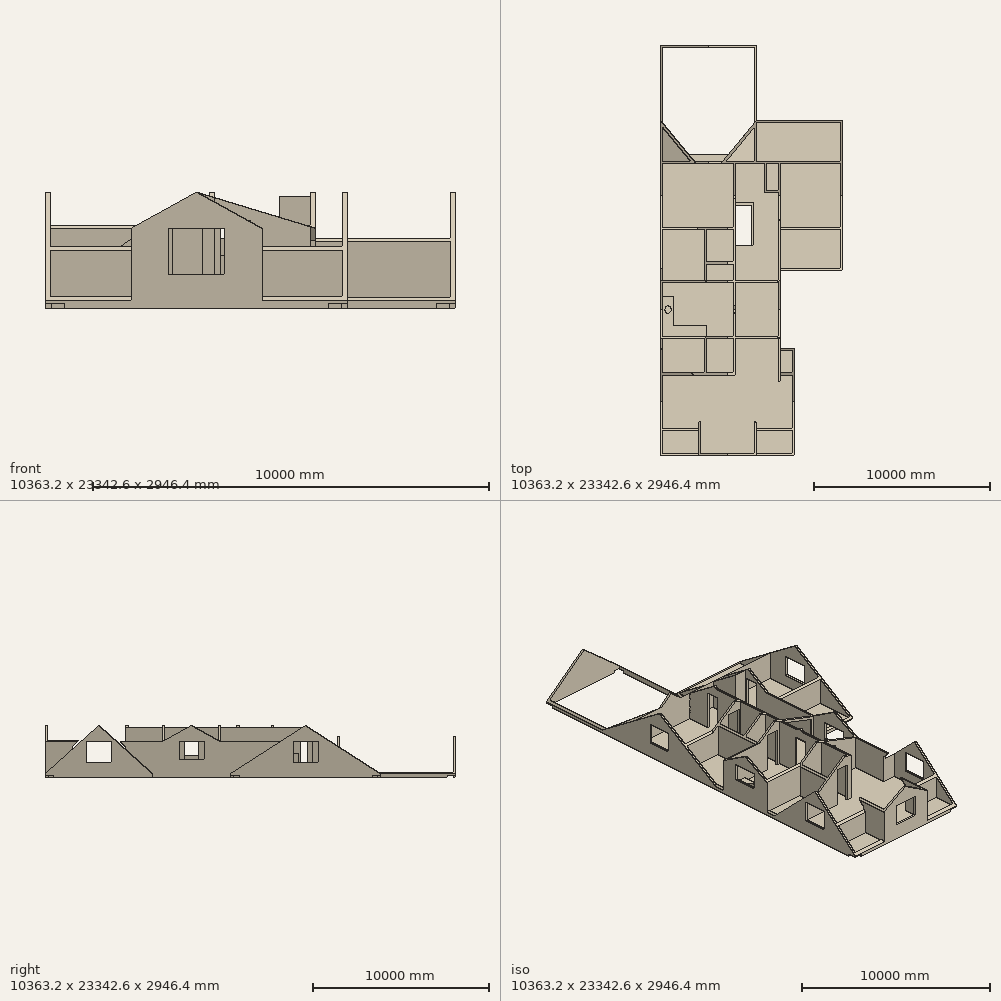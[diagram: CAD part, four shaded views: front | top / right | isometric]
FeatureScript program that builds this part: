
annotation { "Feature Type Name" : "Feature", "Feature Type Description" : "" }
export const myFeature = defineFeature(function(context is Context, id is Id, definition is map)
    precondition{}
    {
        {
            var Q0;
            Q0=qCreatedBy(makeId("Top.planeOp"),FACE);
            cPlane(context, id + "F0", {"entities" : qUnion([Q0]), "cplaneType" : CPlaneType.OFFSET, "offset" : 2946.4 * mm, "width" : 152.4 * mm, "height" : 152.4 * mm});
        }
        {
            var Q0;
            Q0=qCreatedBy(makeId("Top.planeOp"),FACE);
            var sketch = newSketch(context, id + "F1", { "sketchPlane" : qUnion([Q0])});
            skLineSegment(sketch, "E0", {"start": v(0, 0) * mm, "end": v(7645.4, 0) * mm});
            skLineSegment(sketch, "E1", {"start": v(7645.4, 0) * mm, "end": v(7645.4, 6096) * mm});
            skLineSegment(sketch, "E2", {"start": v(7645.4, 6096) * mm, "end": v(6832.6, 6096) * mm});
            skLineSegment(sketch, "E3", {"start": v(6832.6, 6096) * mm, "end": v(6832.6, 10541) * mm});
            skLineSegment(sketch, "E4", {"start": v(6832.6, 10541) * mm, "end": v(10363.2, 10541) * mm});
            skLineSegment(sketch, "E5", {"start": v(10363.2, 10541) * mm, "end": v(10363.2, 19075.4) * mm});
            skLineSegment(sketch, "E6", {"start": v(10363.2, 19075.4) * mm, "end": v(5486.4, 19075.4) * mm});
            skLineSegment(sketch, "E7", {"start": v(5486.4, 19075.4) * mm, "end": v(5486.4, 23342.6) * mm});
            skLineSegment(sketch, "E8", {"start": v(5486.4, 23342.6) * mm, "end": v(0, 23342.6) * mm});
            skLineSegment(sketch, "E9", {"start": v(0, 23342.6) * mm, "end": v(0, 0) * mm});
            skSolve(sketch);
        }
        {
            var Q0;
            Q0 = qSketchRegion(id + "F1", true);
            extrude(context, id + "F2", {"entities" : qUnion([Q0]), "depth" : 2946.4 * mm});
        }
        {
            var Q0;
            Q0=makeQuery(id+"F2.opExtrude","SWEPT_FACE",FACE,{"disambiguationData":[OSD([sQuery(id+"F1.wireOp",EDGE,"E5")])]});
            var sketch = newSketch(context, id + "F3", { "sketchPlane" : qUnion([Q0])});
            skLineSegment(sketch, "E10", {"start": v(10541, 203.2) * mm, "end": v(19075.4, 203.2) * mm, "construction": true});
            skLineSegment(sketch, "E11", {"start": v(14808.2, 203.2) * mm, "end": v(14808.2, 2946.4) * mm, "construction": true});
            skLineSegment(sketch, "E12", {"start": v(10541, 203.2) * mm, "end": v(14808.2, 2946.4) * mm});
            skLineSegment(sketch, "E13", {"start": v(10541, 203.2) * mm, "end": v(10541, 2946.4) * mm});
            skLineSegment(sketch, "E14", {"start": v(10541, 2946.4) * mm, "end": v(19075.4, 2946.4) * mm});
            skLineSegment(sketch, "E15", {"start": v(19075.4, 2946.4) * mm, "end": v(19075.4, 203.2) * mm});
            skLineSegment(sketch, "E16", {"start": v(19075.4, 203.2) * mm, "end": v(14808.2, 2946.4) * mm});
            skLineSegment(sketch, "E17", {"start": v(6096, 203.2) * mm, "end": v(0, 203.2) * mm, "construction": true});
            skLineSegment(sketch, "E18", {"start": v(3048, 203.2) * mm, "end": v(3048, 2946.4) * mm, "construction": true});
            skLineSegment(sketch, "E19", {"start": v(3048, 2946.4) * mm, "end": v(0, 203.2) * mm});
            skLineSegment(sketch, "E20", {"start": v(0, 203.2) * mm, "end": v(0, 2946.4) * mm});
            skLineSegment(sketch, "E21", {"start": v(0, 2946.4) * mm, "end": v(6096, 2946.4) * mm});
            skLineSegment(sketch, "E22", {"start": v(6096, 2946.4) * mm, "end": v(6096, 203.2) * mm});
            skLineSegment(sketch, "E23", {"start": v(6096, 203.2) * mm, "end": v(3048, 2946.4) * mm});
            skSolve(sketch);
        }
        {
            var Q0;
            Q0 = qSketchRegion(id + "F3", true);
            extrude(context, id + "F4", {"entities" : qUnion([Q0]), "operationType" : NewBodyOperationType.REMOVE, "endBound" : BoundingType.THROUGH_ALL, "oppositeDirection" : true, "depth" : 25.4 * mm});
        }
        {
            var Q0;
            Q0=makeQuery(id+"F2.opExtrude","SWEPT_FACE",FACE,{"disambiguationData":[OSD([sQuery(id+"F1.wireOp",EDGE,"E8")])]});
            var sketch = newSketch(context, id + "F5", { "sketchPlane" : qUnion([Q0])});
            skLineSegment(sketch, "E24", {"start": v(-5486.4, 203.2) * mm, "end": v(0, 203.2) * mm, "construction": true});
            skLineSegment(sketch, "E25", {"start": v(-2743.2, 203.2) * mm, "end": v(-2743.2, 2336.8) * mm, "construction": true});
            skLineSegment(sketch, "E26", {"start": v(-5486.4, 203.2) * mm, "end": v(-2743.2, 2336.8) * mm});
            skLineSegment(sketch, "E27", {"start": v(-2743.2, 2336.8) * mm, "end": v(0, 203.2) * mm});
            skLineSegment(sketch, "E28", {"start": v(-5486.4, 203.2) * mm, "end": v(-5486.4, 2946.4) * mm});
            skLineSegment(sketch, "E29", {"start": v(-5486.4, 2946.4) * mm, "end": v(0, 2946.4) * mm});
            skLineSegment(sketch, "E30", {"start": v(0, 2946.4) * mm, "end": v(0, 203.2) * mm});
            skSolve(sketch);
        }
        {
            var Q0;
            Q0 = qSketchRegion(id + "F5", true);
            extrude(context, id + "F6", {"entities" : qUnion([Q0]), "operationType" : NewBodyOperationType.REMOVE, "oppositeDirection" : true, "depth" : 4267.2 * mm});
        }
        {
            var Q0;
            Q0=makeQuery(id+"F4.boolean.opBoolean","COPY",FACE,{"derivedFrom":makeQuery(id+"F4.opExtrude","SWEPT_FACE",FACE,{"disambiguationData":[OSD([sQuery(id+"F3.wireOp",EDGE,"E15")])]})});
            var sketch = newSketch(context, id + "F7", { "sketchPlane" : qUnion([Q0])});
            skLineSegment(sketch, "E31", {"start": v(0, 203.2) * mm, "end": v(2743.2, 2336.8) * mm});
            skLineSegment(sketch, "E32", {"start": v(2743.2, 2336.8) * mm, "end": v(5486.4, 203.2) * mm});
            skLineSegment(sketch, "E33", {"start": v(5486.4, 203.2) * mm, "end": v(0, 203.2) * mm});
            skSolve(sketch);
        }
        {
            var Q0;
            Q0 = qSketchRegion(id + "F7", true);
            extrude(context, id + "F8", {"entities" : qUnion([Q0]), "operationType" : NewBodyOperationType.ADD, "endBound" : BoundingType.UP_TO_NEXT, "depth" : 25.4 * mm});
        }
        {
            var Q0;
            Q0=makeQuery(id+"F4.boolean.opBoolean","COPY",FACE,{"derivedFrom":makeQuery(id+"F4.opExtrude","SWEPT_FACE",FACE,{"disambiguationData":[OSD([sQuery(id+"F3.wireOp",EDGE,"E22")])]})});
            var sketch = newSketch(context, id + "F9", { "sketchPlane" : qUnion([Q0])});
            skLineSegment(sketch, "E34", {"start": v(0, 203.2) * mm, "end": v(6832.6, 203.2) * mm, "construction": true});
            skLineSegment(sketch, "E35", {"start": v(3822.7, 203.2) * mm, "end": v(3822.7, 2946.4) * mm, "construction": true});
            skLineSegment(sketch, "E36", {"start": v(6832.6, 203.2) * mm, "end": v(6832.6, 2032) * mm, "construction": true});
            skLineSegment(sketch, "E37", {"start": v(0, 203.2) * mm, "end": v(3822.7, 2946.4) * mm});
            skLineSegment(sketch, "E38", {"start": v(3822.7, 2946.4) * mm, "end": v(6832.6, 2032) * mm});
            skLineSegment(sketch, "E39", {"start": v(6832.6, 2032) * mm, "end": v(6832.6, 2946.4) * mm});
            skLineSegment(sketch, "E40", {"start": v(6832.6, 2946.4) * mm, "end": v(0, 2946.4) * mm});
            skLineSegment(sketch, "E41", {"start": v(0, 2946.4) * mm, "end": v(0, 203.2) * mm});
            skSolve(sketch);
        }
        {
            var Q0;
            Q0 = qSketchRegion(id + "F9", true);
            extrude(context, id + "F10", {"entities" : qUnion([Q0]), "operationType" : NewBodyOperationType.REMOVE, "oppositeDirection" : true, "depth" : 4445 * mm});
        }
        {
            var Q0;
            Q0=makeQuery(id+"F4.boolean.opBoolean","COPY",FACE,{"derivedFrom":makeQuery(id+"F4.opExtrude","SWEPT_FACE",FACE,{"disambiguationData":[OSD([sQuery(id+"F3.wireOp",EDGE,"E13")])]})});
            var sketch = newSketch(context, id + "F11", { "sketchPlane" : qUnion([Q0])});
            skLineSegment(sketch, "E42", {"start": v(0, 203.2) * mm, "end": v(-6832.6, 203.2) * mm});
            skLineSegment(sketch, "E43", {"start": v(-6832.6, 203.2) * mm, "end": v(-6832.6, 2032) * mm});
            skLineSegment(sketch, "E44", {"start": v(-6832.6, 2032) * mm, "end": v(-3822.7, 2946.4) * mm});
            skLineSegment(sketch, "E45", {"start": v(-3822.7, 2946.4) * mm, "end": v(0, 203.2) * mm});
            skSolve(sketch);
        }
        {
            var Q0;
            Q0 = qSketchRegion(id + "F11", true);
            extrude(context, id + "F12", {"entities" : qUnion([Q0]), "operationType" : NewBodyOperationType.ADD, "endBound" : BoundingType.UP_TO_NEXT, "depth" : 25.4 * mm});
        }
        {
            var Q0;
            Q0=makeQuery(id+"F4.boolean.opBoolean","COPY",FACE,{"derivedFrom":makeQuery(id+"F4.opExtrude","SWEPT_FACE",FACE,{"disambiguationData":[OSD([sQuery(id+"F3.wireOp",EDGE,"E22")])]})});
            var sketch = newSketch(context, id + "F13", { "sketchPlane" : qUnion([Q0])});
            skLineSegment(sketch, "E46", {"start": v(0, 203.2) * mm, "end": v(3822.7, 2946.4) * mm});
            skLineSegment(sketch, "E47", {"start": v(3822.7, 2946.4) * mm, "end": v(6832.6, 2032) * mm});
            skLineSegment(sketch, "E48", {"start": v(6832.6, 2032) * mm, "end": v(6832.6, 203.2) * mm});
            skLineSegment(sketch, "E49", {"start": v(6832.6, 203.2) * mm, "end": v(0, 203.2) * mm});
            skSolve(sketch);
        }
        {
            var Q0;
            Q0 = qSketchRegion(id + "F13", true);
            extrude(context, id + "F14", {"entities" : qUnion([Q0]), "operationType" : NewBodyOperationType.ADD, "endBound" : BoundingType.UP_TO_NEXT, "depth" : 25.4 * mm});
        }
        {
            var Q0;
            Q0=makeQuery(id+"F14.boolean.opBoolean","MERGE",FACE,{"derivedFrom":[makeQuery(id+"F12.boolean.opBoolean","MERGE",FACE,{"derivedFrom":[makeQuery(id+"F2.opExtrude","SWEPT_FACE",FACE,{"disambiguationData":[OSD([sQuery(id+"F1.wireOp",EDGE,"E3")])]}),makeQuery(id+"F12.opExtrude","SWEPT_FACE",FACE,{"disambiguationData":[OSD([sQuery(id+"F11.wireOp",EDGE,"E43")])]})]}),makeQuery(id+"F14.opExtrude","SWEPT_FACE",FACE,{"disambiguationData":[OSD([sQuery(id+"F13.wireOp",EDGE,"E48")])]})]});
            var sketch = newSketch(context, id + "F15", { "sketchPlane" : qUnion([Q0])});
            skLineSegment(sketch, "E50", {"start": v(6667.5, 203.2) * mm, "end": v(9969.5, 203.2) * mm, "construction": true});
            skLineSegment(sketch, "E51", {"start": v(8318.5, 203.2) * mm, "end": v(8318.5, 2946.4) * mm, "construction": true});
            skLineSegment(sketch, "E52", {"start": v(6667.5, 203.2) * mm, "end": v(6667.5, 2032) * mm, "construction": true});
            skLineSegment(sketch, "E53", {"start": v(6667.5, 2032) * mm, "end": v(8318.5, 2946.4) * mm});
            skLineSegment(sketch, "E54.MirrorCS", {"start": v(9969.5, 2032) * mm, "end": v(8318.5, 2946.4) * mm});
            skLineSegment(sketch, "E55", {"start": v(6667.5, 2032) * mm, "end": v(9969.5, 2032) * mm});
            skSolve(sketch);
        }
        {
            var Q0;
            Q0 = qSketchRegion(id + "F15", true);
            extrude(context, id + "F16", {"entities" : qUnion([Q0]), "operationType" : NewBodyOperationType.ADD, "endBound" : BoundingType.UP_TO_NEXT, "oppositeDirection" : true, "depth" : 25.4 * mm});
        }
        {
            var Q0;
            Q0=makeQuery(id+"F2.opExtrude","SWEPT_FACE",FACE,{"disambiguationData":[OSD([sQuery(id+"F1.wireOp",EDGE,"E9")])]});
            var sketch = newSketch(context, id + "F17", { "sketchPlane" : qUnion([Q0])});
            skLineSegment(sketch, "E56", {"start": v(-9969.5, 203.2) * mm, "end": v(-6667.5, 203.2) * mm});
            skLineSegment(sketch, "E57", {"start": v(-8318.5, 203.2) * mm, "end": v(-8318.5, 2946.4) * mm, "construction": true});
            skLineSegment(sketch, "E58", {"start": v(-9969.5, 203.2) * mm, "end": v(-9969.5, 2032) * mm});
            skLineSegment(sketch, "E59", {"start": v(-9969.5, 2032) * mm, "end": v(-8318.5, 2946.4) * mm});
            skLineSegment(sketch, "E60.MirrorCS", {"start": v(-6667.5, 203.2) * mm, "end": v(-6667.5, 2032) * mm});
            skLineSegment(sketch, "E61.MirrorCS", {"start": v(-6667.5, 2032) * mm, "end": v(-8318.5, 2946.4) * mm});
            skSolve(sketch);
        }
        {
            var Q0;
            Q0 = qSketchRegion(id + "F17", true);
            extrude(context, id + "F18", {"entities" : qUnion([Q0]), "operationType" : NewBodyOperationType.ADD, "endBound" : BoundingType.UP_TO_NEXT, "oppositeDirection" : true, "depth" : 25.4 * mm});
        }
        {
            var Q0;
            Q0=makeQuery(id+"F2.opExtrude","SWEPT_FACE",FACE,{"disambiguationData":[OSD([sQuery(id+"F1.wireOp",EDGE,"E0")])]});
            var sketch = newSketch(context, id + "F19", { "sketchPlane" : qUnion([Q0])});
            skLineSegment(sketch, "E62", {"start": v(2171.7, 203.2) * mm, "end": v(5473.7, 203.2) * mm});
            skLineSegment(sketch, "E63", {"start": v(3822.7, 203.2) * mm, "end": v(3822.7, 2946.4) * mm, "construction": true});
            skLineSegment(sketch, "E64", {"start": v(2171.7, 203.2) * mm, "end": v(2171.7, 2032) * mm});
            skLineSegment(sketch, "E65", {"start": v(2171.7, 2032) * mm, "end": v(3822.7, 2946.4) * mm});
            skLineSegment(sketch, "E66.MirrorCS", {"start": v(5473.7, 203.2) * mm, "end": v(5473.7, 2032) * mm});
            skLineSegment(sketch, "E67.MirrorCS", {"start": v(5473.7, 2032) * mm, "end": v(3822.7, 2946.4) * mm});
            skSolve(sketch);
        }
        {
            var Q0;
            Q0 = qSketchRegion(id + "F19", true);
            extrude(context, id + "F20", {"entities" : qUnion([Q0]), "operationType" : NewBodyOperationType.ADD, "endBound" : BoundingType.UP_TO_NEXT, "oppositeDirection" : true, "depth" : 25.4 * mm});
        }
        {
            var Q0;
            Q0=qCreatedBy(id+"F0.planeOp",FACE);
            var sketch = newSketch(context, id + "F21", { "sketchPlane" : qUnion([Q0])});
            skLineSegment(sketch, "E68.bottom", {"start": v(127, 23215.6) * mm, "end": v(5359.4, 23215.6) * mm});
            skLineSegment(sketch, "E68.top", {"start": v(127, 16764) * mm, "end": v(5359.4, 16764) * mm});
            skLineSegment(sketch, "E68.left", {"start": v(127, 23215.6) * mm, "end": v(127, 16764) * mm});
            skLineSegment(sketch, "E68.right", {"start": v(5359.4, 23215.6) * mm, "end": v(5359.4, 16764) * mm});
            skLineSegment(sketch, "E69.bottom", {"start": v(5486.4, 18948.4) * mm, "end": v(10236.2, 18948.4) * mm});
            skLineSegment(sketch, "E69.top", {"start": v(5486.4, 16764) * mm, "end": v(10236.2, 16764) * mm});
            skLineSegment(sketch, "E69.left", {"start": v(5486.4, 18948.4) * mm, "end": v(5486.4, 16764) * mm});
            skLineSegment(sketch, "E69.right", {"start": v(10236.2, 18948.4) * mm, "end": v(10236.2, 16764) * mm});
            skLineSegment(sketch, "E70.bottom", {"start": v(6832.6, 16637) * mm, "end": v(10236.2, 16637) * mm});
            skLineSegment(sketch, "E70.top", {"start": v(6832.6, 12979.4) * mm, "end": v(10236.2, 12979.4) * mm});
            skLineSegment(sketch, "E70.left", {"start": v(6832.6, 16637) * mm, "end": v(6832.6, 12979.4) * mm});
            skLineSegment(sketch, "E70.right", {"start": v(10236.2, 16637) * mm, "end": v(10236.2, 12979.4) * mm});
            skLineSegment(sketch, "E71.bottom", {"start": v(6832.6, 12852.4) * mm, "end": v(10236.2, 12852.4) * mm});
            skLineSegment(sketch, "E71.top", {"start": v(6832.6, 10668) * mm, "end": v(10236.2, 10668) * mm});
            skLineSegment(sketch, "E71.left", {"start": v(6832.6, 12852.4) * mm, "end": v(6832.6, 10668) * mm});
            skLineSegment(sketch, "E71.right", {"start": v(10236.2, 12852.4) * mm, "end": v(10236.2, 10668) * mm});
            skLineSegment(sketch, "E72.bottom", {"start": v(6032.5, 16637) * mm, "end": v(6705.6, 16637) * mm});
            skLineSegment(sketch, "E72.top", {"start": v(6032.5, 15113) * mm, "end": v(6705.6, 15113) * mm});
            skLineSegment(sketch, "E72.left", {"start": v(6032.5, 16637) * mm, "end": v(6032.5, 15113) * mm});
            skLineSegment(sketch, "E72.right", {"start": v(6705.6, 16637) * mm, "end": v(6705.6, 15113) * mm});
            skLineSegment(sketch, "E73.bottom", {"start": v(127, 16637) * mm, "end": v(4140.2, 16637) * mm});
            skLineSegment(sketch, "E73.top", {"start": v(127, 12979.4) * mm, "end": v(4140.2, 12979.4) * mm});
            skLineSegment(sketch, "E73.left", {"start": v(127, 16637) * mm, "end": v(127, 12979.4) * mm});
            skLineSegment(sketch, "E73.right", {"start": v(4140.2, 16637) * mm, "end": v(4140.2, 12979.4) * mm});
            skLineSegment(sketch, "E74.bottom", {"start": v(127, 12852.4) * mm, "end": v(2489.2, 12852.4) * mm});
            skLineSegment(sketch, "E74.top", {"start": v(127, 9969.5) * mm, "end": v(2489.2, 9969.5) * mm});
            skLineSegment(sketch, "E74.left", {"start": v(127, 12852.4) * mm, "end": v(127, 9969.5) * mm});
            skLineSegment(sketch, "E74.right", {"start": v(2489.2, 12852.4) * mm, "end": v(2489.2, 9969.5) * mm});
            skLineSegment(sketch, "E75.bottom", {"start": v(2616.2, 12852.4) * mm, "end": v(4140.2, 12852.4) * mm});
            skLineSegment(sketch, "E75.top", {"start": v(2616.2, 11023.6) * mm, "end": v(4140.2, 11023.6) * mm});
            skLineSegment(sketch, "E75.left", {"start": v(2616.2, 12852.4) * mm, "end": v(2616.2, 11023.6) * mm});
            skLineSegment(sketch, "E75.right", {"start": v(4140.2, 12852.4) * mm, "end": v(4140.2, 11023.6) * mm});
            skLineSegment(sketch, "E76.bottom", {"start": v(2616.2, 10896.6) * mm, "end": v(4140.2, 10896.6) * mm});
            skLineSegment(sketch, "E76.top", {"start": v(2616.2, 9969.5) * mm, "end": v(4140.2, 9969.5) * mm});
            skLineSegment(sketch, "E76.left", {"start": v(2616.2, 10896.6) * mm, "end": v(2616.2, 9969.5) * mm});
            skLineSegment(sketch, "E76.right", {"start": v(4140.2, 10896.6) * mm, "end": v(4140.2, 9969.5) * mm});
            skLineSegment(sketch, "E77.bottom", {"start": v(127, 9842.5) * mm, "end": v(4140.2, 9842.5) * mm});
            skLineSegment(sketch, "E77.top", {"start": v(127, 6794.5) * mm, "end": v(4140.2, 6794.5) * mm});
            skLineSegment(sketch, "E77.left", {"start": v(127, 9842.5) * mm, "end": v(127, 6794.5) * mm});
            skLineSegment(sketch, "E77.right", {"start": v(4140.2, 9842.5) * mm, "end": v(4140.2, 6794.5) * mm});
            skLineSegment(sketch, "E78.bottom", {"start": v(127, 6667.5) * mm, "end": v(2489.2, 6667.5) * mm});
            skLineSegment(sketch, "E78.top", {"start": v(127, 4699) * mm, "end": v(2489.2, 4699) * mm});
            skLineSegment(sketch, "E78.left", {"start": v(127, 6667.5) * mm, "end": v(127, 4699) * mm});
            skLineSegment(sketch, "E78.right", {"start": v(2489.2, 6667.5) * mm, "end": v(2489.2, 4699) * mm});
            skLineSegment(sketch, "E79.bottom", {"start": v(2616.2, 6667.5) * mm, "end": v(4140.2, 6667.5) * mm});
            skLineSegment(sketch, "E79.top", {"start": v(2616.2, 4699) * mm, "end": v(4140.2, 4699) * mm});
            skLineSegment(sketch, "E79.left", {"start": v(2616.2, 6667.5) * mm, "end": v(2616.2, 4699) * mm});
            skLineSegment(sketch, "E79.right", {"start": v(4140.2, 6667.5) * mm, "end": v(4140.2, 4699) * mm});
            skLineSegment(sketch, "E80.bottom", {"start": v(127, 1397) * mm, "end": v(2171.7, 1397) * mm});
            skLineSegment(sketch, "E80.top", {"start": v(127, 127) * mm, "end": v(2171.7, 127) * mm});
            skLineSegment(sketch, "E80.left", {"start": v(127, 1397) * mm, "end": v(127, 127) * mm});
            skLineSegment(sketch, "E80.right", {"start": v(2171.7, 1397) * mm, "end": v(2171.7, 127) * mm});
            skLineSegment(sketch, "E81.bottom", {"start": v(5473.7, 1397) * mm, "end": v(7518.4, 1397) * mm});
            skLineSegment(sketch, "E81.top", {"start": v(5473.7, 127) * mm, "end": v(7518.4, 127) * mm});
            skLineSegment(sketch, "E81.left", {"start": v(5473.7, 1397) * mm, "end": v(5473.7, 127) * mm});
            skLineSegment(sketch, "E81.right", {"start": v(7518.4, 1397) * mm, "end": v(7518.4, 127) * mm});
            skLineSegment(sketch, "E82.bottom", {"start": v(6832.6, 5969) * mm, "end": v(7518.4, 5969) * mm});
            skLineSegment(sketch, "E82.top", {"start": v(6832.6, 4699) * mm, "end": v(7518.4, 4699) * mm});
            skLineSegment(sketch, "E82.left", {"start": v(6832.6, 5969) * mm, "end": v(6832.6, 4699) * mm});
            skLineSegment(sketch, "E82.right", {"start": v(7518.4, 5969) * mm, "end": v(7518.4, 4699) * mm});
            skLineSegment(sketch, "E83", {"start": v(127, 4572) * mm, "end": v(127, 1524) * mm});
            skLineSegment(sketch, "E84", {"start": v(127, 1524) * mm, "end": v(2298.7, 1524) * mm});
            skLineSegment(sketch, "E85", {"start": v(7518.4, 1524) * mm, "end": v(7518.4, 4572) * mm});
            skLineSegment(sketch, "E86", {"start": v(7518.4, 4572) * mm, "end": v(6705.6, 4572) * mm});
            skLineSegment(sketch, "E87", {"start": v(6705.6, 4572) * mm, "end": v(6705.6, 6667.5) * mm});
            skLineSegment(sketch, "E88", {"start": v(6705.6, 6667.5) * mm, "end": v(4267.2, 6667.5) * mm});
            skLineSegment(sketch, "E89", {"start": v(4267.2, 6667.5) * mm, "end": v(4267.2, 4572) * mm});
            skLineSegment(sketch, "E90", {"start": v(4267.2, 4572) * mm, "end": v(127, 4572) * mm});
            skLineSegment(sketch, "E91", {"start": v(4267.2, 16637) * mm, "end": v(4267.2, 9969.5) * mm});
            skLineSegment(sketch, "E92", {"start": v(4267.2, 6794.5) * mm, "end": v(6705.6, 6794.5) * mm});
            skLineSegment(sketch, "E93", {"start": v(6705.6, 6794.5) * mm, "end": v(6705.6, 9842.5) * mm});
            skLineSegment(sketch, "E94", {"start": v(6705.6, 14986) * mm, "end": v(5905.5, 14986) * mm});
            skLineSegment(sketch, "E95", {"start": v(5905.5, 14986) * mm, "end": v(5905.5, 16637) * mm});
            skLineSegment(sketch, "E96", {"start": v(5905.5, 16637) * mm, "end": v(4267.2, 16637) * mm});
            skLineSegment(sketch, "E97", {"start": v(2298.7, 1524) * mm, "end": v(2298.7, 127) * mm});
            skLineSegment(sketch, "E98", {"start": v(2298.7, 127) * mm, "end": v(5346.7, 127) * mm});
            skLineSegment(sketch, "E99", {"start": v(5346.7, 127) * mm, "end": v(5346.7, 1524) * mm});
            skLineSegment(sketch, "E100.trimOffspring", {"start": v(5346.7, 1524) * mm, "end": v(7518.4, 1524) * mm});
            skLineSegment(sketch, "E101", {"start": v(4267.2, 9842.5) * mm, "end": v(6705.6, 9842.5) * mm});
            skLineSegment(sketch, "E102", {"start": v(6705.6, 9969.5) * mm, "end": v(4267.2, 9969.5) * mm});
            skLineSegment(sketch, "E103.trimOffspring", {"start": v(4267.2, 9842.5) * mm, "end": v(4267.2, 6794.5) * mm});
            skLineSegment(sketch, "E104.trimOffspring", {"start": v(6705.6, 9969.5) * mm, "end": v(6705.6, 14986) * mm});
            skSolve(sketch);
        }
        {
            var Q0;
            Q0 = qSketchRegion(id + "F21", true);
            extrude(context, id + "F22", {"entities" : qUnion([Q0]), "operationType" : NewBodyOperationType.REMOVE, "oppositeDirection" : true, "depth" : 2743.2 * mm});
        }
        {
            var Q0;
            Q0=makeQuery(id+"F22.boolean.opBoolean","COPY",FACE,{"derivedFrom":makeQuery(id+"F22.opExtrude","SWEPT_FACE",FACE,{"disambiguationData":[OSD([sQuery(id+"F21.wireOp",EDGE,"E100.trimOffspring")])]})});
            var sketch = newSketch(context, id + "F23", { "sketchPlane" : qUnion([Q0])});
            skLineSegment(sketch, "E105", {"start": v(-5346.7, 1727.2) * mm, "end": v(-5473.7, 1727.2) * mm});
            skLineSegment(sketch, "E106", {"start": v(-5473.7, 1727.2) * mm, "end": v(-5473.7, 2032) * mm});
            skLineSegment(sketch, "E107", {"start": v(-5473.7, 2032) * mm, "end": v(-5346.7, 2102.34) * mm});
            skLineSegment(sketch, "E108", {"start": v(-5346.7, 2102.34) * mm, "end": v(-5346.7, 1727.2) * mm});
            skLineSegment(sketch, "E109", {"start": v(-2298.7, 1727.2) * mm, "end": v(-2171.7, 1727.2) * mm});
            skLineSegment(sketch, "E110", {"start": v(-2171.7, 1727.2) * mm, "end": v(-2171.7, 2032) * mm});
            skLineSegment(sketch, "E111", {"start": v(-2171.7, 2032) * mm, "end": v(-2298.7, 2102.34) * mm});
            skLineSegment(sketch, "E112", {"start": v(-2298.7, 2102.34) * mm, "end": v(-2298.7, 1727.2) * mm});
            skSolve(sketch);
        }
        {
            var Q0;
            Q0 = qSketchRegion(id + "F23", true);
            extrude(context, id + "F24", {"entities" : qUnion([Q0]), "operationType" : NewBodyOperationType.ADD, "depth" : 609.6 * mm});
        }
        {
            var Q0;
            Q0=makeQuery(id+"F24.boolean.opBoolean","MERGE",FACE,{"derivedFrom":[makeQuery(id+"F22.boolean.opBoolean","MERGE",FACE,{"derivedFrom":[makeQuery(id+"F20.opExtrude","SWEPT_FACE",FACE,{"disambiguationData":[OSD([sQuery(id+"F19.wireOp",EDGE,"E66.MirrorCS")])]}),makeQuery(id+"F22.opExtrude","SWEPT_FACE",FACE,{"disambiguationData":[OSD([sQuery(id+"F21.wireOp",EDGE,"E81.left")])]})]}),makeQuery(id+"F24.opExtrude","SWEPT_FACE",FACE,{"disambiguationData":[OSD([sQuery(id+"F23.wireOp",EDGE,"E106")])]})]});
            var sketch = newSketch(context, id + "F25", { "sketchPlane" : qUnion([Q0])});
            skLineSegment(sketch, "E113", {"start": v(1524, 1727.2) * mm, "end": v(1940.82, 2102.34) * mm});
            skLineSegment(sketch, "E114", {"start": v(1940.82, 2102.34) * mm, "end": v(2133.6, 2102.34) * mm});
            skLineSegment(sketch, "E115", {"start": v(2133.6, 2102.34) * mm, "end": v(2133.6, 1727.2) * mm});
            skLineSegment(sketch, "E116", {"start": v(2133.6, 1727.2) * mm, "end": v(1524, 1727.2) * mm});
            skSolve(sketch);
        }
        {
            var Q0;
            Q0 = qSketchRegion(id + "F25", true);
            var Q1;
            Q1=makeQuery(id+"F24.boolean.opBoolean","MERGE",FACE,{"derivedFrom":[makeQuery(id+"F22.boolean.opBoolean","MERGE",FACE,{"derivedFrom":[makeQuery(id+"F20.opExtrude","SWEPT_FACE",FACE,{"disambiguationData":[OSD([sQuery(id+"F19.wireOp",EDGE,"E64")])]}),makeQuery(id+"F22.opExtrude","SWEPT_FACE",FACE,{"disambiguationData":[OSD([sQuery(id+"F21.wireOp",EDGE,"E80.right")])]})]}),makeQuery(id+"F24.opExtrude","SWEPT_FACE",FACE,{"disambiguationData":[OSD([sQuery(id+"F23.wireOp",EDGE,"E110")])]})]});
            extrude(context, id + "F26", {"entities" : qUnion([Q0]), "operationType" : NewBodyOperationType.REMOVE, "endBound" : BoundingType.UP_TO_SURFACE, "oppositeDirection" : true, "endBoundEntityFace" : qUnion([Q1]), "depth" : 25.4 * mm});
        }
        {
            var Q0;
            Q0=makeQuery(id+"F22.boolean.opBoolean","COPY",FACE,{"derivedFrom":makeQuery(id+"F22.opExtrude","SWEPT_FACE",FACE,{"disambiguationData":[OSD([sQuery(id+"F21.wireOp",EDGE,"E86")])]})});
            var sketch = newSketch(context, id + "F27", { "sketchPlane" : qUnion([Q0])});
            skLineSegment(sketch, "E117", {"start": v(6705.6, 1727.2) * mm, "end": v(6832.6, 1727.2) * mm});
            skLineSegment(sketch, "E118", {"start": v(6832.6, 1727.2) * mm, "end": v(6832.6, 2032) * mm});
            skLineSegment(sketch, "E119", {"start": v(6832.6, 2032) * mm, "end": v(6705.6, 2070.58) * mm});
            skLineSegment(sketch, "E120", {"start": v(6705.6, 2070.58) * mm, "end": v(6705.6, 1727.2) * mm});
            skSolve(sketch);
        }
        {
            var Q0;
            Q0 = qSketchRegion(id + "F27", true);
            extrude(context, id + "F28", {"entities" : qUnion([Q0]), "operationType" : NewBodyOperationType.ADD, "depth" : 609.6 * mm});
        }
        {
            var Q0;
            Q0=makeQuery(id+"F28.boolean.opBoolean","MERGE",FACE,{"derivedFrom":[makeQuery(id+"F22.boolean.opBoolean","MERGE",FACE,{"derivedFrom":[makeQuery(id+"F16.boolean.opBoolean","MERGE",FACE,{"derivedFrom":[makeQuery(id+"F14.boolean.opBoolean","MERGE",FACE,{"derivedFrom":[makeQuery(id+"F12.boolean.opBoolean","MERGE",FACE,{"derivedFrom":[makeQuery(id+"F2.opExtrude","SWEPT_FACE",FACE,{"disambiguationData":[OSD([sQuery(id+"F1.wireOp",EDGE,"E3")])]}),makeQuery(id+"F12.opExtrude","SWEPT_FACE",FACE,{"disambiguationData":[OSD([sQuery(id+"F11.wireOp",EDGE,"E43")])]})]}),makeQuery(id+"F14.opExtrude","SWEPT_FACE",FACE,{"disambiguationData":[OSD([sQuery(id+"F13.wireOp",EDGE,"E48")])]})]}),makeQuery(id+"F16.opExtrude","CAP_FACE",FACE,{"disambiguationData":[OSD([sQuery(id+"F15.wireOp",EDGE,"E53"),sQuery(id+"F15.wireOp",EDGE,"E54.MirrorCS"),sQuery(id+"F15.wireOp",EDGE,"E55")])],"isStart":true})]}),makeQuery(id+"F22.opExtrude","SWEPT_FACE",FACE,{"disambiguationData":[OSD([sQuery(id+"F21.wireOp",EDGE,"E70.left")])]}),makeQuery(id+"F22.opExtrude","SWEPT_FACE",FACE,{"disambiguationData":[OSD([sQuery(id+"F21.wireOp",EDGE,"E71.left")])]}),makeQuery(id+"F22.opExtrude","SWEPT_FACE",FACE,{"disambiguationData":[OSD([sQuery(id+"F21.wireOp",EDGE,"E82.left")])]})]}),makeQuery(id+"F28.opExtrude","SWEPT_FACE",FACE,{"disambiguationData":[OSD([sQuery(id+"F27.wireOp",EDGE,"E118")])]})]});
            var sketch = newSketch(context, id + "F29", { "sketchPlane" : qUnion([Q0])});
            skLineSegment(sketch, "E121", {"start": v(4572, 1727.2) * mm, "end": v(4190.46, 2070.58) * mm});
            skLineSegment(sketch, "E122", {"start": v(4190.46, 2070.58) * mm, "end": v(3962.4, 2070.58) * mm});
            skLineSegment(sketch, "E123", {"start": v(3962.4, 2070.58) * mm, "end": v(3962.4, 1727.2) * mm});
            skLineSegment(sketch, "E124", {"start": v(3962.4, 1727.2) * mm, "end": v(4572, 1727.2) * mm});
            skSolve(sketch);
        }
        {
            var Q0;
            Q0 = qSketchRegion(id + "F29", true);
            extrude(context, id + "F30", {"entities" : qUnion([Q0]), "operationType" : NewBodyOperationType.REMOVE, "endBound" : BoundingType.UP_TO_NEXT, "oppositeDirection" : true, "depth" : 25.4 * mm});
        }
        {
            var Q0;
            Q0=makeQuery(id+"F22.boolean.opBoolean","COPY",FACE,{"derivedFrom":makeQuery(id+"F22.opExtrude","CAP_FACE",FACE,{"disambiguationData":[OSD([sQuery(id+"F21.wireOp",EDGE,"E68.bottom"),sQuery(id+"F21.wireOp",EDGE,"E68.top"),sQuery(id+"F21.wireOp",EDGE,"E68.left"),sQuery(id+"F21.wireOp",EDGE,"E68.right")])],"isStart":false})});
            var sketch = newSketch(context, id + "F31", { "sketchPlane" : qUnion([Q0])});
            skLineSegment(sketch, "E125.bottom", {"start": v(127, 23215.6) * mm, "end": v(5359.4, 23215.6) * mm});
            skLineSegment(sketch, "E125.top", {"start": v(127, 17119.6) * mm, "end": v(5359.4, 17119.6) * mm});
            skLineSegment(sketch, "E125.left", {"start": v(127, 23215.6) * mm, "end": v(127, 17119.6) * mm});
            skLineSegment(sketch, "E125.right", {"start": v(5359.4, 23215.6) * mm, "end": v(5359.4, 17119.6) * mm});
            skSolve(sketch);
        }
        {
            var Q0;
            Q0 = qSketchRegion(id + "F31", true);
            extrude(context, id + "F32", {"entities" : qUnion([Q0]), "operationType" : NewBodyOperationType.REMOVE, "endBound" : BoundingType.UP_TO_NEXT, "oppositeDirection" : true, "depth" : 25.4 * mm});
        }
        {
            var Q0;
            Q0=makeQuery(id+"F22.boolean.opBoolean","COPY",FACE,{"derivedFrom":makeQuery(id+"F22.opExtrude","CAP_FACE",FACE,{"disambiguationData":[OSD([sQuery(id+"F21.wireOp",EDGE,"E91"),sQuery(id+"F21.wireOp",EDGE,"E94"),sQuery(id+"F21.wireOp",EDGE,"E95"),sQuery(id+"F21.wireOp",EDGE,"E96"),sQuery(id+"F21.wireOp",EDGE,"E102"),sQuery(id+"F21.wireOp",EDGE,"E104.trimOffspring")])],"isStart":false})});
            var sketch = newSketch(context, id + "F33", { "sketchPlane" : qUnion([Q0])});
            skLineSegment(sketch, "E126.bottom", {"start": v(4267.2, 11963.4) * mm, "end": v(5181.6, 11963.4) * mm});
            skLineSegment(sketch, "E126.top", {"start": v(4267.2, 14249.4) * mm, "end": v(5181.6, 14249.4) * mm});
            skLineSegment(sketch, "E126.left", {"start": v(4267.2, 11963.4) * mm, "end": v(4267.2, 14249.4) * mm});
            skLineSegment(sketch, "E126.right", {"start": v(5181.6, 11963.4) * mm, "end": v(5181.6, 14249.4) * mm});
            skSolve(sketch);
        }
        {
            var Q0;
            Q0 = qSketchRegion(id + "F33", true);
            extrude(context, id + "F34", {"entities" : qUnion([Q0]), "operationType" : NewBodyOperationType.REMOVE, "endBound" : BoundingType.UP_TO_NEXT, "oppositeDirection" : true, "depth" : 25.4 * mm});
        }
        {
            var Q0;
            Q0=makeQuery(id+"F22.boolean.opBoolean","COPY",FACE,{"derivedFrom":makeQuery(id+"F22.opExtrude","CAP_FACE",FACE,{"disambiguationData":[OSD([sQuery(id+"F21.wireOp",EDGE,"E91"),sQuery(id+"F21.wireOp",EDGE,"E94"),sQuery(id+"F21.wireOp",EDGE,"E95"),sQuery(id+"F21.wireOp",EDGE,"E96"),sQuery(id+"F21.wireOp",EDGE,"E102"),sQuery(id+"F21.wireOp",EDGE,"E104.trimOffspring")])],"isStart":false})});
            var sketch = newSketch(context, id + "F35", { "sketchPlane" : qUnion([Q0])});
            skLineSegment(sketch, "E127", {"start": v(4267.2, 14249.4) * mm, "end": v(5181.6, 14249.4) * mm});
            skLineSegment(sketch, "E128", {"start": v(5181.6, 14249.4) * mm, "end": v(5181.6, 11963.4) * mm});
            skLineSegment(sketch, "E129", {"start": v(5181.6, 11963.4) * mm, "end": v(5308.6, 11963.4) * mm});
            skLineSegment(sketch, "E130", {"start": v(5308.6, 11963.4) * mm, "end": v(5308.6, 14376.4) * mm});
            skLineSegment(sketch, "E131", {"start": v(5308.6, 14376.4) * mm, "end": v(4267.2, 14376.4) * mm});
            skLineSegment(sketch, "E132", {"start": v(4267.2, 14376.4) * mm, "end": v(4267.2, 14249.4) * mm});
            skSolve(sketch);
        }
        {
            var Q0;
            Q0 = qSketchRegion(id + "F35", true);
            extrude(context, id + "F36", {"entities" : qUnion([Q0]), "operationType" : NewBodyOperationType.ADD, "depth" : 1143 * mm});
        }
        {
            var Q0;
            Q0=makeQuery(id+"F34.boolean.opBoolean","MERGE",FACE,{"derivedFrom":[makeQuery(id+"F22.boolean.opBoolean","COPY",FACE,{"derivedFrom":makeQuery(id+"F22.opExtrude","SWEPT_FACE",FACE,{"disambiguationData":[OSD([sQuery(id+"F21.wireOp",EDGE,"E91")])]})}),makeQuery(id+"F34.opExtrude","SWEPT_FACE",FACE,{"disambiguationData":[OSD([sQuery(id+"F33.wireOp",EDGE,"E126.left")])]})]});
            var sketch = newSketch(context, id + "F37", { "sketchPlane" : qUnion([Q0])});
            skLineSegment(sketch, "E133", {"start": v(14249.4, 0) * mm, "end": v(14503.4, 0) * mm});
            skLineSegment(sketch, "E134", {"start": v(14503.4, 0) * mm, "end": v(14249.4, 203.2) * mm});
            skLineSegment(sketch, "E135", {"start": v(14249.4, 203.2) * mm, "end": v(14249.4, 0) * mm});
            skSolve(sketch);
        }
        {
            var Q0;
            Q0 = qSketchRegion(id + "F37", true);
            extrude(context, id + "F38", {"entities" : qUnion([Q0]), "operationType" : NewBodyOperationType.REMOVE, "depth" : 914.4 * mm});
        }
        {
            var Q0;
            Q0=makeQuery(id+"F22.boolean.opBoolean","SPLIT",FACE,{"disambiguationData":[TD([makeQuery(id+"F2.opExtrude","SWEPT_FACE",FACE,{"disambiguationData":[OSD([sQuery(id+"F1.wireOp",EDGE,"E6")])]})])],"derivedFrom":makeQuery(id+"F8.boolean.opBoolean","MERGE",FACE,{"derivedFrom":[makeQuery(id+"F6.boolean.opBoolean","COPY",FACE,{"derivedFrom":makeQuery(id+"F6.opExtrude","SWEPT_FACE",FACE,{"disambiguationData":[OSD([sQuery(id+"F5.wireOp",EDGE,"E26")])]})}),makeQuery(id+"F8.opExtrude","SWEPT_FACE",FACE,{"disambiguationData":[OSD([sQuery(id+"F7.wireOp",EDGE,"E32")])]})]})});
            var sketch = newSketch(context, id + "F39", { "sketchPlane" : qUnion([Q0])});
            skLineSegment(sketch, "E136", {"start": v(4045.06, 18921.75) * mm, "end": v(1785.68, 16764) * mm});
            skLineSegment(sketch, "E137", {"start": v(1785.68, 16764) * mm, "end": v(4045.06, 16764) * mm});
            skLineSegment(sketch, "E138", {"start": v(4045.06, 16764) * mm, "end": v(4045.06, 18921.75) * mm});
            skSolve(sketch);
        }
        {
            var Q0;
            Q0 = qSketchRegion(id + "F39", true);
            extrude(context, id + "F40", {"entities" : qUnion([Q0]), "operationType" : NewBodyOperationType.ADD, "depth" : 127 * mm});
        }
        {
            var Q0;
            Q0=makeQuery(id+"F22.boolean.opBoolean","SPLIT",FACE,{"disambiguationData":[TD([makeQuery(id+"F2.opExtrude","SWEPT_FACE",FACE,{"disambiguationData":[OSD([sQuery(id+"F1.wireOp",EDGE,"E8")])]})])],"derivedFrom":makeQuery(id+"F8.boolean.opBoolean","MERGE",FACE,{"derivedFrom":[makeQuery(id+"F6.boolean.opBoolean","COPY",FACE,{"derivedFrom":makeQuery(id+"F6.opExtrude","SWEPT_FACE",FACE,{"disambiguationData":[OSD([sQuery(id+"F5.wireOp",EDGE,"E27")])]})}),makeQuery(id+"F8.opExtrude","SWEPT_FACE",FACE,{"disambiguationData":[OSD([sQuery(id+"F7.wireOp",EDGE,"E31")])]})]})});
            var sketch = newSketch(context, id + "F41", { "sketchPlane" : qUnion([Q0])});
            skLineSegment(sketch, "E139", {"start": v(285.64, 18921.75) * mm, "end": v(2545.02, 16764) * mm});
            skLineSegment(sketch, "E140", {"start": v(2545.02, 16764) * mm, "end": v(285.64, 16764) * mm});
            skLineSegment(sketch, "E141", {"start": v(285.64, 16764) * mm, "end": v(285.64, 18921.75) * mm});
            skSolve(sketch);
        }
        {
            var Q0;
            Q0 = qSketchRegion(id + "F41", true);
            extrude(context, id + "F42", {"entities" : qUnion([Q0]), "operationType" : NewBodyOperationType.ADD, "depth" : 127 * mm});
        }
        {
            var Q0;
            Q0=makeQuery(id+"F22.boolean.opBoolean","SPLIT",FACE,{"disambiguationData":[TD([makeQuery(id+"F2.opExtrude","SWEPT_FACE",FACE,{"disambiguationData":[OSD([sQuery(id+"F1.wireOp",EDGE,"E3")])]})])],"derivedFrom":makeQuery(id+"F4.boolean.opBoolean","COPY",FACE,{"derivedFrom":makeQuery(id+"F4.opExtrude","SWEPT_FACE",FACE,{"disambiguationData":[OSD([sQuery(id+"F3.wireOp",EDGE,"E16")])]})})});
            var sketch = newSketch(context, id + "F43", { "sketchPlane" : qUnion([Q0])});
            skLineSegment(sketch, "E142", {"start": v(5431.9, 15857.54) * mm, "end": v(3503.46, 13083.85) * mm});
            skLineSegment(sketch, "E143", {"start": v(3503.46, 13083.85) * mm, "end": v(3642.91, 12986.9) * mm});
            skLineSegment(sketch, "E144", {"start": v(3642.91, 12986.9) * mm, "end": v(5571.35, 15760.59) * mm});
            skLineSegment(sketch, "E145", {"start": v(5571.35, 15760.59) * mm, "end": v(5431.9, 15857.54) * mm});
            skLineSegment(sketch, "E146", {"start": v(2743.2, 13324.2) * mm, "end": v(2743.2, 15864.2) * mm, "construction": true});
            skLineSegment(sketch, "E147.MirrorCS", {"start": v(-84.95, 15760.59) * mm, "end": v(54.5, 15857.54) * mm});
            skLineSegment(sketch, "E148.MirrorCS", {"start": v(1982.94, 13083.85) * mm, "end": v(1843.49, 12986.9) * mm});
            skLineSegment(sketch, "E149.MirrorCS", {"start": v(54.5, 15857.54) * mm, "end": v(1982.94, 13083.85) * mm});
            skLineSegment(sketch, "E150.MirrorCS", {"start": v(1843.49, 12986.9) * mm, "end": v(-84.95, 15760.59) * mm});
            skSolve(sketch);
        }
        {
            var Q0;
            Q0 = qSketchRegion(id + "F43", true);
            extrude(context, id + "F44", {"entities" : qUnion([Q0]), "operationType" : NewBodyOperationType.REMOVE, "endBound" : BoundingType.UP_TO_NEXT, "depth" : 25.4 * mm});
        }
        {
            var Q0;
            Q0=makeQuery(id+"F22.boolean.opBoolean","COPY",FACE,{"derivedFrom":makeQuery(id+"F22.opExtrude","SWEPT_FACE",FACE,{"disambiguationData":[OSD([sQuery(id+"F21.wireOp",EDGE,"E98")])]})});
            var sketch = newSketch(context, id + "F45", { "sketchPlane" : qUnion([Q0])});
            skLineSegment(sketch, "E151", {"start": v(-3822.7, 2946.4) * mm, "end": v(-3822.7, 203.2) * mm, "construction": true});
            skLineSegment(sketch, "E152.bottom", {"start": v(-4533.9, 2032) * mm, "end": v(-3111.5, 2032) * mm});
            skLineSegment(sketch, "E152.top", {"start": v(-4533.9, 863.6) * mm, "end": v(-3111.5, 863.6) * mm});
            skLineSegment(sketch, "E152.left", {"start": v(-4533.9, 2032) * mm, "end": v(-4533.9, 863.6) * mm});
            skLineSegment(sketch, "E152.right", {"start": v(-3111.5, 2032) * mm, "end": v(-3111.5, 863.6) * mm});
            skSolve(sketch);
        }
        {
            var Q0;
            Q0 = qSketchRegion(id + "F45", true);
            extrude(context, id + "F46", {"entities" : qUnion([Q0]), "operationType" : NewBodyOperationType.REMOVE, "endBound" : BoundingType.UP_TO_NEXT, "oppositeDirection" : true, "depth" : 25.4 * mm});
        }
        {
            var Q0;
            Q0=makeQuery(id+"F22.boolean.opBoolean","COPY",FACE,{"derivedFrom":makeQuery(id+"F22.opExtrude","SWEPT_FACE",FACE,{"disambiguationData":[OSD([sQuery(id+"F21.wireOp",EDGE,"E83")])]})});
            var sketch = newSketch(context, id + "F47", { "sketchPlane" : qUnion([Q0])});
            skLineSegment(sketch, "E153", {"start": v(3048, 2946.4) * mm, "end": v(3048, 203.2) * mm, "construction": true});
            skLineSegment(sketch, "E154.bottom", {"start": v(2336.8, 2032) * mm, "end": v(3759.2, 2032) * mm});
            skLineSegment(sketch, "E154.top", {"start": v(2336.8, 863.6) * mm, "end": v(3759.2, 863.6) * mm});
            skLineSegment(sketch, "E154.left", {"start": v(2336.8, 2032) * mm, "end": v(2336.8, 863.6) * mm});
            skLineSegment(sketch, "E154.right", {"start": v(3759.2, 2032) * mm, "end": v(3759.2, 863.6) * mm});
            skSolve(sketch);
        }
        {
            var Q0;
            Q0 = qSketchRegion(id + "F47", true);
            extrude(context, id + "F48", {"entities" : qUnion([Q0]), "operationType" : NewBodyOperationType.REMOVE, "endBound" : BoundingType.UP_TO_NEXT, "oppositeDirection" : true, "depth" : 25.4 * mm});
        }
        {
            var Q0;
            Q0=makeQuery(id+"F22.boolean.opBoolean","COPY",FACE,{"derivedFrom":makeQuery(id+"F22.opExtrude","SWEPT_FACE",FACE,{"disambiguationData":[OSD([sQuery(id+"F21.wireOp",EDGE,"E85")])]})});
            var sketch = newSketch(context, id + "F49", { "sketchPlane" : qUnion([Q0])});
            skLineSegment(sketch, "E155", {"start": v(-3048, 2946.4) * mm, "end": v(-3048, 203.2) * mm, "construction": true});
            skLineSegment(sketch, "E156.bottom", {"start": v(-3759.2, 2032) * mm, "end": v(-2336.8, 2032) * mm});
            skLineSegment(sketch, "E156.top", {"start": v(-3759.2, 863.6) * mm, "end": v(-2336.8, 863.6) * mm});
            skLineSegment(sketch, "E156.left", {"start": v(-3759.2, 2032) * mm, "end": v(-3759.2, 863.6) * mm});
            skLineSegment(sketch, "E156.right", {"start": v(-2336.8, 2032) * mm, "end": v(-2336.8, 863.6) * mm});
            skSolve(sketch);
        }
        {
            var Q0;
            Q0 = qSketchRegion(id + "F49", true);
            extrude(context, id + "F50", {"entities" : qUnion([Q0]), "operationType" : NewBodyOperationType.REMOVE, "endBound" : BoundingType.UP_TO_NEXT, "oppositeDirection" : true, "depth" : 25.4 * mm});
        }
        {
            var Q0;
            Q0=makeQuery(id+"F22.boolean.opBoolean","COPY",FACE,{"derivedFrom":makeQuery(id+"F22.opExtrude","SWEPT_FACE",FACE,{"disambiguationData":[OSD([sQuery(id+"F21.wireOp",EDGE,"E77.left")])]})});
            var sketch = newSketch(context, id + "F51", { "sketchPlane" : qUnion([Q0])});
            skLineSegment(sketch, "E157", {"start": v(8318.5, 2946.4) * mm, "end": v(8318.5, 203.2) * mm, "construction": true});
            skLineSegment(sketch, "E158.bottom", {"start": v(7607.3, 2159) * mm, "end": v(9029.7, 2159) * mm});
            skLineSegment(sketch, "E158.top", {"start": v(7607.3, 1244.6) * mm, "end": v(9029.7, 1244.6) * mm});
            skLineSegment(sketch, "E158.left", {"start": v(7607.3, 2159) * mm, "end": v(7607.3, 1244.6) * mm});
            skLineSegment(sketch, "E158.right", {"start": v(9029.7, 2159) * mm, "end": v(9029.7, 1244.6) * mm});
            skSolve(sketch);
        }
        {
            var Q0;
            Q0 = qSketchRegion(id + "F51", true);
            extrude(context, id + "F52", {"entities" : qUnion([Q0]), "operationType" : NewBodyOperationType.REMOVE, "endBound" : BoundingType.UP_TO_NEXT, "oppositeDirection" : true, "depth" : 25.4 * mm});
        }
        {
            var Q0;
            Q0=makeQuery(id+"F22.boolean.opBoolean","COPY",FACE,{"derivedFrom":makeQuery(id+"F22.opExtrude","SWEPT_FACE",FACE,{"disambiguationData":[OSD([sQuery(id+"F21.wireOp",EDGE,"E93")])]})});
            var sketch = newSketch(context, id + "F53", { "sketchPlane" : qUnion([Q0])});
            skLineSegment(sketch, "E159", {"start": v(-8318.5, 2946.4) * mm, "end": v(-8318.5, 203.2) * mm, "construction": true});
            skLineSegment(sketch, "E160.bottom", {"start": v(-9029.7, 2032) * mm, "end": v(-7607.3, 2032) * mm});
            skLineSegment(sketch, "E160.top", {"start": v(-9029.7, 1016) * mm, "end": v(-7607.3, 1016) * mm});
            skLineSegment(sketch, "E160.left", {"start": v(-9029.7, 2032) * mm, "end": v(-9029.7, 1016) * mm});
            skLineSegment(sketch, "E160.right", {"start": v(-7607.3, 2032) * mm, "end": v(-7607.3, 1016) * mm});
            skSolve(sketch);
        }
        {
            var Q0;
            Q0 = qSketchRegion(id + "F53", true);
            extrude(context, id + "F54", {"entities" : qUnion([Q0]), "operationType" : NewBodyOperationType.REMOVE, "endBound" : BoundingType.UP_TO_NEXT, "oppositeDirection" : true, "depth" : 25.4 * mm});
        }
        {
            var Q0;
            Q0=makeQuery(id+"F22.boolean.opBoolean","COPY",FACE,{"derivedFrom":makeQuery(id+"F22.opExtrude","SWEPT_FACE",FACE,{"disambiguationData":[OSD([sQuery(id+"F21.wireOp",EDGE,"E73.left")])]})});
            var sketch = newSketch(context, id + "F55", { "sketchPlane" : qUnion([Q0])});
            skLineSegment(sketch, "E161", {"start": v(14808.2, 2946.4) * mm, "end": v(14808.2, 203.2) * mm, "construction": true});
            skLineSegment(sketch, "E162.bottom", {"start": v(14097, 2032) * mm, "end": v(15519.4, 2032) * mm});
            skLineSegment(sketch, "E162.top", {"start": v(14097, 863.6) * mm, "end": v(15519.4, 863.6) * mm});
            skLineSegment(sketch, "E162.left", {"start": v(14097, 2032) * mm, "end": v(14097, 863.6) * mm});
            skLineSegment(sketch, "E162.right", {"start": v(15519.4, 2032) * mm, "end": v(15519.4, 863.6) * mm});
            skSolve(sketch);
        }
        {
            var Q0;
            Q0 = qSketchRegion(id + "F55", true);
            extrude(context, id + "F56", {"entities" : qUnion([Q0]), "operationType" : NewBodyOperationType.REMOVE, "endBound" : BoundingType.UP_TO_NEXT, "oppositeDirection" : true, "depth" : 25.4 * mm});
        }
        {
            var Q0;
            Q0=makeQuery(id+"F22.boolean.opBoolean","COPY",FACE,{"derivedFrom":makeQuery(id+"F22.opExtrude","SWEPT_FACE",FACE,{"disambiguationData":[OSD([sQuery(id+"F21.wireOp",EDGE,"E70.right")])]})});
            var sketch = newSketch(context, id + "F57", { "sketchPlane" : qUnion([Q0])});
            skLineSegment(sketch, "E163", {"start": v(-14808.2, 2946.4) * mm, "end": v(-14808.2, 203.2) * mm, "construction": true});
            skLineSegment(sketch, "E164.bottom", {"start": v(-15519.4, 2032) * mm, "end": v(-14097, 2032) * mm});
            skLineSegment(sketch, "E164.top", {"start": v(-15519.4, 863.6) * mm, "end": v(-14097, 863.6) * mm});
            skLineSegment(sketch, "E164.left", {"start": v(-15519.4, 2032) * mm, "end": v(-15519.4, 863.6) * mm});
            skLineSegment(sketch, "E164.right", {"start": v(-14097, 2032) * mm, "end": v(-14097, 863.6) * mm});
            skSolve(sketch);
        }
        {
            var Q0;
            Q0 = qSketchRegion(id + "F57", true);
            extrude(context, id + "F58", {"entities" : qUnion([Q0]), "operationType" : NewBodyOperationType.REMOVE, "endBound" : BoundingType.UP_TO_NEXT, "oppositeDirection" : true, "depth" : 25.4 * mm});
        }
        {
            var Q0;
            Q0=makeQuery(id+"F22.boolean.opBoolean","COPY",FACE,{"derivedFrom":makeQuery(id+"F22.opExtrude","SWEPT_FACE",FACE,{"disambiguationData":[OSD([sQuery(id+"F21.wireOp",EDGE,"E90")])]})});
            var sketch = newSketch(context, id + "F59", { "sketchPlane" : qUnion([Q0])});
            skLineSegment(sketch, "E165.bottom", {"start": v(3962.4, 203.2) * mm, "end": v(3200.4, 203.2) * mm});
            skLineSegment(sketch, "E165.top", {"start": v(3962.4, 2336.8) * mm, "end": v(3200.4, 2336.8) * mm});
            skLineSegment(sketch, "E165.left", {"start": v(3962.4, 203.2) * mm, "end": v(3962.4, 2336.8) * mm});
            skLineSegment(sketch, "E165.right", {"start": v(3200.4, 203.2) * mm, "end": v(3200.4, 2336.8) * mm});
            skSolve(sketch);
        }
        {
            var Q0;
            Q0 = qSketchRegion(id + "F59", true);
            extrude(context, id + "F60", {"entities" : qUnion([Q0]), "operationType" : NewBodyOperationType.REMOVE, "endBound" : BoundingType.UP_TO_NEXT, "oppositeDirection" : true, "depth" : 25.4 * mm});
        }
        {
            var Q0;
            Q0=makeQuery(id+"F22.boolean.opBoolean","COPY",FACE,{"derivedFrom":makeQuery(id+"F22.opExtrude","SWEPT_FACE",FACE,{"disambiguationData":[OSD([sQuery(id+"F21.wireOp",EDGE,"E88")])]})});
            var sketch = newSketch(context, id + "F61", { "sketchPlane" : qUnion([Q0])});
            skLineSegment(sketch, "E166.bottom", {"start": v(4419.6, 203.2) * mm, "end": v(5181.6, 203.2) * mm});
            skLineSegment(sketch, "E166.top", {"start": v(4419.6, 2235.2) * mm, "end": v(5181.6, 2235.2) * mm});
            skLineSegment(sketch, "E166.left", {"start": v(4419.6, 203.2) * mm, "end": v(4419.6, 2235.2) * mm});
            skLineSegment(sketch, "E166.right", {"start": v(5181.6, 203.2) * mm, "end": v(5181.6, 2235.2) * mm});
            skSolve(sketch);
        }
        {
            var Q0;
            Q0 = qSketchRegion(id + "F61", true);
            extrude(context, id + "F62", {"entities" : qUnion([Q0]), "operationType" : NewBodyOperationType.REMOVE, "endBound" : BoundingType.UP_TO_NEXT, "oppositeDirection" : true, "depth" : 25.4 * mm});
        }
        {
            var Q0;
            Q0=makeQuery(id+"F22.boolean.opBoolean","COPY",FACE,{"derivedFrom":makeQuery(id+"F22.opExtrude","SWEPT_FACE",FACE,{"disambiguationData":[OSD([sQuery(id+"F21.wireOp",EDGE,"E101")])]})});
            var sketch = newSketch(context, id + "F63", { "sketchPlane" : qUnion([Q0])});
            skLineSegment(sketch, "E167", {"start": v(6553.2, 203.2) * mm, "end": v(4419.6, 203.2) * mm});
            skLineSegment(sketch, "E168", {"start": v(4419.6, 203.2) * mm, "end": v(4419.6, 2605.79) * mm});
            skLineSegment(sketch, "E169", {"start": v(4419.6, 2605.79) * mm, "end": v(6553.2, 1957.6) * mm});
            skLineSegment(sketch, "E170", {"start": v(6553.2, 1957.6) * mm, "end": v(6553.2, 203.2) * mm});
            skSolve(sketch);
        }
        {
            var Q0;
            Q0 = qSketchRegion(id + "F63", true);
            extrude(context, id + "F64", {"entities" : qUnion([Q0]), "operationType" : NewBodyOperationType.REMOVE, "endBound" : BoundingType.UP_TO_NEXT, "oppositeDirection" : true, "depth" : 25.4 * mm});
        }
        {
            var Q0;
            Q0=makeQuery(id+"F22.boolean.opBoolean","COPY",FACE,{"derivedFrom":makeQuery(id+"F22.opExtrude","SWEPT_FACE",FACE,{"disambiguationData":[OSD([sQuery(id+"F21.wireOp",EDGE,"E77.right")])]})});
            var sketch = newSketch(context, id + "F65", { "sketchPlane" : qUnion([Q0])});
            skLineSegment(sketch, "E171", {"start": v(-8318.5, 2946.4) * mm, "end": v(-8318.5, 203.2) * mm, "construction": true});
            skLineSegment(sketch, "E172.bottom", {"start": v(-8699.5, 203.2) * mm, "end": v(-7937.5, 203.2) * mm});
            skLineSegment(sketch, "E172.top", {"start": v(-8699.5, 2336.8) * mm, "end": v(-7937.5, 2336.8) * mm});
            skLineSegment(sketch, "E172.left", {"start": v(-8699.5, 203.2) * mm, "end": v(-8699.5, 2336.8) * mm});
            skLineSegment(sketch, "E172.right", {"start": v(-7937.5, 203.2) * mm, "end": v(-7937.5, 2336.8) * mm});
            skSolve(sketch);
        }
        {
            var Q0;
            Q0 = qSketchRegion(id + "F65", true);
            extrude(context, id + "F66", {"entities" : qUnion([Q0]), "operationType" : NewBodyOperationType.REMOVE, "endBound" : BoundingType.UP_TO_NEXT, "oppositeDirection" : true, "depth" : 25.4 * mm});
        }
        {
            var Q0;
            Q0=makeQuery(id+"F22.boolean.opBoolean","COPY",FACE,{"derivedFrom":makeQuery(id+"F22.opExtrude","SWEPT_FACE",FACE,{"disambiguationData":[OSD([sQuery(id+"F21.wireOp",EDGE,"E77.bottom")])]})});
            var sketch = newSketch(context, id + "F67", { "sketchPlane" : qUnion([Q0])});
            skLineSegment(sketch, "E173.bottom", {"start": v(3200.4, 203.2) * mm, "end": v(3962.4, 203.2) * mm});
            skLineSegment(sketch, "E173.top", {"start": v(3200.4, 2336.8) * mm, "end": v(3962.4, 2336.8) * mm});
            skLineSegment(sketch, "E173.left", {"start": v(3200.4, 203.2) * mm, "end": v(3200.4, 2336.8) * mm});
            skLineSegment(sketch, "E173.right", {"start": v(3962.4, 203.2) * mm, "end": v(3962.4, 2336.8) * mm});
            skSolve(sketch);
        }
        {
            var Q0;
            Q0 = qSketchRegion(id + "F67", true);
            extrude(context, id + "F68", {"entities" : qUnion([Q0]), "operationType" : NewBodyOperationType.REMOVE, "endBound" : BoundingType.UP_TO_NEXT, "oppositeDirection" : true, "depth" : 25.4 * mm});
        }
        {
            var Q0;
            Q0=makeQuery(id+"F28.boolean.opBoolean","MERGE",FACE,{"derivedFrom":[makeQuery(id+"F22.boolean.opBoolean","MERGE",FACE,{"derivedFrom":[makeQuery(id+"F16.boolean.opBoolean","MERGE",FACE,{"derivedFrom":[makeQuery(id+"F14.boolean.opBoolean","MERGE",FACE,{"derivedFrom":[makeQuery(id+"F12.boolean.opBoolean","MERGE",FACE,{"derivedFrom":[makeQuery(id+"F2.opExtrude","SWEPT_FACE",FACE,{"disambiguationData":[OSD([sQuery(id+"F1.wireOp",EDGE,"E3")])]}),makeQuery(id+"F12.opExtrude","SWEPT_FACE",FACE,{"disambiguationData":[OSD([sQuery(id+"F11.wireOp",EDGE,"E43")])]})]}),makeQuery(id+"F14.opExtrude","SWEPT_FACE",FACE,{"disambiguationData":[OSD([sQuery(id+"F13.wireOp",EDGE,"E48")])]})]}),makeQuery(id+"F16.opExtrude","CAP_FACE",FACE,{"disambiguationData":[OSD([sQuery(id+"F15.wireOp",EDGE,"E53"),sQuery(id+"F15.wireOp",EDGE,"E54.MirrorCS"),sQuery(id+"F15.wireOp",EDGE,"E55")])],"isStart":true})]}),makeQuery(id+"F22.opExtrude","SWEPT_FACE",FACE,{"disambiguationData":[OSD([sQuery(id+"F21.wireOp",EDGE,"E70.left")])]}),makeQuery(id+"F22.opExtrude","SWEPT_FACE",FACE,{"disambiguationData":[OSD([sQuery(id+"F21.wireOp",EDGE,"E71.left")])]}),makeQuery(id+"F22.opExtrude","SWEPT_FACE",FACE,{"disambiguationData":[OSD([sQuery(id+"F21.wireOp",EDGE,"E82.left")])]})]}),makeQuery(id+"F28.opExtrude","SWEPT_FACE",FACE,{"disambiguationData":[OSD([sQuery(id+"F27.wireOp",EDGE,"E118")])]})]});
            var sketch = newSketch(context, id + "F69", { "sketchPlane" : qUnion([Q0])});
            skLineSegment(sketch, "E174.bottom", {"start": v(15189.2, 203.2) * mm, "end": v(15951.2, 203.2) * mm});
            skLineSegment(sketch, "E174.top", {"start": v(15189.2, 2032) * mm, "end": v(15951.2, 2032) * mm});
            skLineSegment(sketch, "E174.left", {"start": v(15189.2, 203.2) * mm, "end": v(15189.2, 2032) * mm});
            skLineSegment(sketch, "E174.right", {"start": v(15951.2, 203.2) * mm, "end": v(15951.2, 2032) * mm});
            skLineSegment(sketch, "E175.bottom", {"start": v(14909.8, 203.2) * mm, "end": v(14147.8, 203.2) * mm});
            skLineSegment(sketch, "E175.top", {"start": v(14909.8, 2336.8) * mm, "end": v(14147.8, 2336.8) * mm});
            skLineSegment(sketch, "E175.left", {"start": v(14909.8, 203.2) * mm, "end": v(14909.8, 2336.8) * mm});
            skLineSegment(sketch, "E175.right", {"start": v(14147.8, 203.2) * mm, "end": v(14147.8, 2336.8) * mm});
            skSolve(sketch);
        }
        {
            var Q0;
            Q0 = qSketchRegion(id + "F69", true);
            extrude(context, id + "F70", {"entities" : qUnion([Q0]), "operationType" : NewBodyOperationType.REMOVE, "endBound" : BoundingType.UP_TO_NEXT, "oppositeDirection" : true, "depth" : 25.4 * mm});
        }
        {
            var Q0;
            Q0=makeQuery(id+"F38.boolean.opBoolean","MERGE",FACE,{"derivedFrom":[makeQuery(id+"F34.boolean.opBoolean","MERGE",FACE,{"derivedFrom":[makeQuery(id+"F22.boolean.opBoolean","COPY",FACE,{"derivedFrom":makeQuery(id+"F22.opExtrude","SWEPT_FACE",FACE,{"disambiguationData":[OSD([sQuery(id+"F21.wireOp",EDGE,"E91")])]})}),makeQuery(id+"F34.opExtrude","SWEPT_FACE",FACE,{"disambiguationData":[OSD([sQuery(id+"F33.wireOp",EDGE,"E126.left")])]})]}),makeQuery(id+"F38.opExtrude","CAP_FACE",FACE,{"disambiguationData":[OSD([sQuery(id+"F37.wireOp",EDGE,"E133"),sQuery(id+"F37.wireOp",EDGE,"E134"),sQuery(id+"F37.wireOp",EDGE,"E135")])],"isStart":true})]});
            var sketch = newSketch(context, id + "F71", { "sketchPlane" : qUnion([Q0])});
            skLineSegment(sketch, "E176.bottom", {"start": v(14528.8, 203.2) * mm, "end": v(15290.8, 203.2) * mm});
            skLineSegment(sketch, "E176.top", {"start": v(14528.8, 2336.8) * mm, "end": v(15290.8, 2336.8) * mm});
            skLineSegment(sketch, "E176.left", {"start": v(14528.8, 203.2) * mm, "end": v(14528.8, 2336.8) * mm});
            skLineSegment(sketch, "E176.right", {"start": v(15290.8, 203.2) * mm, "end": v(15290.8, 2336.8) * mm});
            skSolve(sketch);
        }
        {
            var Q0;
            Q0 = qSketchRegion(id + "F71", true);
            extrude(context, id + "F72", {"entities" : qUnion([Q0]), "operationType" : NewBodyOperationType.REMOVE, "endBound" : BoundingType.UP_TO_NEXT, "oppositeDirection" : true, "depth" : 25.4 * mm});
        }
        {
            var Q0;
            Q0=makeQuery(id+"F22.boolean.opBoolean","COPY",FACE,{"derivedFrom":makeQuery(id+"F22.opExtrude","SWEPT_FACE",FACE,{"disambiguationData":[OSD([sQuery(id+"F21.wireOp",EDGE,"E73.top")])]})});
            var sketch = newSketch(context, id + "F73", { "sketchPlane" : qUnion([Q0])});
            skLineSegment(sketch, "E177.bottom", {"start": v(-4064, 203.2) * mm, "end": v(-3302, 203.2) * mm});
            skLineSegment(sketch, "E177.top", {"start": v(-4064, 2336.8) * mm, "end": v(-3302, 2336.8) * mm});
            skLineSegment(sketch, "E177.left", {"start": v(-4064, 203.2) * mm, "end": v(-4064, 2336.8) * mm});
            skLineSegment(sketch, "E177.right", {"start": v(-3302, 203.2) * mm, "end": v(-3302, 2336.8) * mm});
            skSolve(sketch);
        }
        {
            var Q0;
            Q0 = qSketchRegion(id + "F73", true);
            extrude(context, id + "F74", {"entities" : qUnion([Q0]), "operationType" : NewBodyOperationType.REMOVE, "endBound" : BoundingType.UP_TO_NEXT, "oppositeDirection" : true, "depth" : 25.4 * mm});
        }
        {
            var Q0;
            Q0=makeQuery(id+"F74.boolean.opBoolean","MERGE",FACE,{"derivedFrom":[makeQuery(id+"F22.boolean.opBoolean","COPY",FACE,{"derivedFrom":makeQuery(id+"F22.opExtrude","CAP_FACE",FACE,{"disambiguationData":[OSD([sQuery(id+"F21.wireOp",EDGE,"E75.bottom"),sQuery(id+"F21.wireOp",EDGE,"E75.top"),sQuery(id+"F21.wireOp",EDGE,"E75.left"),sQuery(id+"F21.wireOp",EDGE,"E75.right")])],"isStart":false})}),makeQuery(id+"F72.boolean.opBoolean","MERGE",FACE,{"derivedFrom":[makeQuery(id+"F22.boolean.opBoolean","COPY",FACE,{"derivedFrom":makeQuery(id+"F22.opExtrude","CAP_FACE",FACE,{"disambiguationData":[OSD([sQuery(id+"F21.wireOp",EDGE,"E73.bottom"),sQuery(id+"F21.wireOp",EDGE,"E73.top"),sQuery(id+"F21.wireOp",EDGE,"E73.left"),sQuery(id+"F21.wireOp",EDGE,"E73.right")])],"isStart":false})}),makeQuery(id+"F70.boolean.opBoolean","MERGE",FACE,{"derivedFrom":[makeQuery(id+"F22.boolean.opBoolean","COPY",FACE,{"derivedFrom":makeQuery(id+"F22.opExtrude","CAP_FACE",FACE,{"disambiguationData":[OSD([sQuery(id+"F21.wireOp",EDGE,"E70.bottom"),sQuery(id+"F21.wireOp",EDGE,"E70.top"),sQuery(id+"F21.wireOp",EDGE,"E70.left"),sQuery(id+"F21.wireOp",EDGE,"E70.right")])],"isStart":false})}),makeQuery(id+"F22.boolean.opBoolean","COPY",FACE,{"derivedFrom":makeQuery(id+"F22.opExtrude","CAP_FACE",FACE,{"disambiguationData":[OSD([sQuery(id+"F21.wireOp",EDGE,"E72.bottom"),sQuery(id+"F21.wireOp",EDGE,"E72.top"),sQuery(id+"F21.wireOp",EDGE,"E72.left"),sQuery(id+"F21.wireOp",EDGE,"E72.right")])],"isStart":false})}),makeQuery(id+"F68.boolean.opBoolean","MERGE",FACE,{"derivedFrom":[makeQuery(id+"F22.boolean.opBoolean","COPY",FACE,{"derivedFrom":makeQuery(id+"F22.opExtrude","CAP_FACE",FACE,{"disambiguationData":[OSD([sQuery(id+"F21.wireOp",EDGE,"E76.bottom"),sQuery(id+"F21.wireOp",EDGE,"E76.top"),sQuery(id+"F21.wireOp",EDGE,"E76.left"),sQuery(id+"F21.wireOp",EDGE,"E76.right")])],"isStart":false})}),makeQuery(id+"F66.boolean.opBoolean","MERGE",FACE,{"derivedFrom":[makeQuery(id+"F22.boolean.opBoolean","COPY",FACE,{"derivedFrom":makeQuery(id+"F22.opExtrude","CAP_FACE",FACE,{"disambiguationData":[OSD([sQuery(id+"F21.wireOp",EDGE,"E77.bottom"),sQuery(id+"F21.wireOp",EDGE,"E77.top"),sQuery(id+"F21.wireOp",EDGE,"E77.left"),sQuery(id+"F21.wireOp",EDGE,"E77.right")])],"isStart":false})}),makeQuery(id+"F64.boolean.opBoolean","MERGE",FACE,{"derivedFrom":[makeQuery(id+"F22.boolean.opBoolean","COPY",FACE,{"derivedFrom":makeQuery(id+"F22.opExtrude","CAP_FACE",FACE,{"disambiguationData":[OSD([sQuery(id+"F21.wireOp",EDGE,"E91"),sQuery(id+"F21.wireOp",EDGE,"E94"),sQuery(id+"F21.wireOp",EDGE,"E95"),sQuery(id+"F21.wireOp",EDGE,"E96"),sQuery(id+"F21.wireOp",EDGE,"E102"),sQuery(id+"F21.wireOp",EDGE,"E104.trimOffspring")])],"isStart":false})}),makeQuery(id+"F62.boolean.opBoolean","MERGE",FACE,{"derivedFrom":[makeQuery(id+"F22.boolean.opBoolean","COPY",FACE,{"derivedFrom":makeQuery(id+"F22.opExtrude","CAP_FACE",FACE,{"disambiguationData":[OSD([sQuery(id+"F21.wireOp",EDGE,"E92"),sQuery(id+"F21.wireOp",EDGE,"E93"),sQuery(id+"F21.wireOp",EDGE,"E101"),sQuery(id+"F21.wireOp",EDGE,"E103.trimOffspring")])],"isStart":false})}),makeQuery(id+"F60.boolean.opBoolean","MERGE",FACE,{"derivedFrom":[makeQuery(id+"F22.boolean.opBoolean","COPY",FACE,{"derivedFrom":makeQuery(id+"F22.opExtrude","CAP_FACE",FACE,{"disambiguationData":[OSD([sQuery(id+"F21.wireOp",EDGE,"E79.bottom"),sQuery(id+"F21.wireOp",EDGE,"E79.top"),sQuery(id+"F21.wireOp",EDGE,"E79.left"),sQuery(id+"F21.wireOp",EDGE,"E79.right")])],"isStart":false})}),makeQuery(id+"F22.boolean.opBoolean","COPY",FACE,{"derivedFrom":makeQuery(id+"F22.opExtrude","CAP_FACE",FACE,{"disambiguationData":[OSD([sQuery(id+"F21.wireOp",EDGE,"E83"),sQuery(id+"F21.wireOp",EDGE,"E84"),sQuery(id+"F21.wireOp",EDGE,"E85"),sQuery(id+"F21.wireOp",EDGE,"E86"),sQuery(id+"F21.wireOp",EDGE,"E87"),sQuery(id+"F21.wireOp",EDGE,"E88"),sQuery(id+"F21.wireOp",EDGE,"E89"),sQuery(id+"F21.wireOp",EDGE,"E90"),sQuery(id+"F21.wireOp",EDGE,"E97"),sQuery(id+"F21.wireOp",EDGE,"E98"),sQuery(id+"F21.wireOp",EDGE,"E99"),sQuery(id+"F21.wireOp",EDGE,"E100.trimOffspring")])],"isStart":false})}),makeQuery(id+"F60.opExtrude","SWEPT_FACE",FACE,{"disambiguationData":[OSD([sQuery(id+"F59.wireOp",EDGE,"E165.bottom")])]})]}),makeQuery(id+"F62.opExtrude","SWEPT_FACE",FACE,{"disambiguationData":[OSD([sQuery(id+"F61.wireOp",EDGE,"E166.bottom")])]})]}),makeQuery(id+"F64.opExtrude","SWEPT_FACE",FACE,{"disambiguationData":[OSD([sQuery(id+"F63.wireOp",EDGE,"E167")])]})]}),makeQuery(id+"F66.opExtrude","SWEPT_FACE",FACE,{"disambiguationData":[OSD([sQuery(id+"F65.wireOp",EDGE,"E172.bottom")])]})]}),makeQuery(id+"F68.opExtrude","SWEPT_FACE",FACE,{"disambiguationData":[OSD([sQuery(id+"F67.wireOp",EDGE,"E173.bottom")])]})]}),makeQuery(id+"F70.opExtrude","SWEPT_FACE",FACE,{"disambiguationData":[OSD([sQuery(id+"F69.wireOp",EDGE,"E174.bottom")])]}),makeQuery(id+"F70.opExtrude","SWEPT_FACE",FACE,{"disambiguationData":[OSD([sQuery(id+"F69.wireOp",EDGE,"E175.bottom")])]})]}),makeQuery(id+"F72.opExtrude","SWEPT_FACE",FACE,{"disambiguationData":[OSD([sQuery(id+"F71.wireOp",EDGE,"E176.bottom")])]})]}),makeQuery(id+"F74.opExtrude","SWEPT_FACE",FACE,{"disambiguationData":[OSD([sQuery(id+"F73.wireOp",EDGE,"E177.bottom")])]})]});
            var sketch = newSketch(context, id + "F75", { "sketchPlane" : qUnion([Q0])});
            skLineSegment(sketch, "E178", {"start": v(127, 9080.5) * mm, "end": v(736.6, 9080.5) * mm});
            skLineSegment(sketch, "E179", {"start": v(736.6, 9080.5) * mm, "end": v(736.6, 7404.1) * mm});
            skLineSegment(sketch, "E180", {"start": v(736.6, 7404.1) * mm, "end": v(2616.2, 7404.1) * mm});
            skLineSegment(sketch, "E181", {"start": v(2616.2, 7404.1) * mm, "end": v(2616.2, 6794.5) * mm});
            skLineSegment(sketch, "E182", {"start": v(2616.2, 6794.5) * mm, "end": v(127, 6794.5) * mm});
            skLineSegment(sketch, "E183", {"start": v(127, 6794.5) * mm, "end": v(127, 9080.5) * mm});
            skSolve(sketch);
        }
        {
            var Q0;
            Q0 = qSketchRegion(id + "F75", true);
            extrude(context, id + "F76", {"entities" : qUnion([Q0]), "operationType" : NewBodyOperationType.ADD, "depth" : 838.2 * mm});
        }
        {
            var Q0;
            Q0=makeQuery(id+"F76.opExtrude","CAP_FACE",FACE,{"disambiguationData":[OSD([sQuery(id+"F75.wireOp",EDGE,"E178"),sQuery(id+"F75.wireOp",EDGE,"E179"),sQuery(id+"F75.wireOp",EDGE,"E180"),sQuery(id+"F75.wireOp",EDGE,"E181"),sQuery(id+"F75.wireOp",EDGE,"E182"),sQuery(id+"F75.wireOp",EDGE,"E183")])],"isStart":false});
            var sketch = newSketch(context, id + "F77", { "sketchPlane" : qUnion([Q0])});
            skLineSegment(sketch, "E184", {"start": v(127, 8293.1) * mm, "end": v(736.6, 8293.1) * mm, "construction": true});
            skEllipse(sketch, "E185", {"center": v(431.8, 8293.1) * mm, "majorRadius": 228.6 * mm, "minorRadius": 177.8 * mm, "majorAxis": v(0, -1)});
            skSolve(sketch);
        }
        {
            var Q0;
            Q0 = qSketchRegion(id + "F77", true);
            extrude(context, id + "F78", {"entities" : qUnion([Q0]), "operationType" : NewBodyOperationType.REMOVE, "oppositeDirection" : true, "depth" : 304.8 * mm});
        }
        {
            var Q0;
            Q0=makeQuery(id+"F2.opExtrude","CAP_FACE",FACE,{"disambiguationData":[OSD([sQuery(id+"F1.wireOp",EDGE,"E0"),sQuery(id+"F1.wireOp",EDGE,"E1"),sQuery(id+"F1.wireOp",EDGE,"E2"),sQuery(id+"F1.wireOp",EDGE,"E3"),sQuery(id+"F1.wireOp",EDGE,"E4"),sQuery(id+"F1.wireOp",EDGE,"E5"),sQuery(id+"F1.wireOp",EDGE,"E6"),sQuery(id+"F1.wireOp",EDGE,"E7"),sQuery(id+"F1.wireOp",EDGE,"E8"),sQuery(id+"F1.wireOp",EDGE,"E9")])],"isStart":true});
            var sketch = newSketch(context, id + "F79", { "sketchPlane" : qUnion([Q0])});
            skLineSegment(sketch, "E186", {"start": v(0, 0) * mm, "end": v(0, -482.6) * mm});
            skLineSegment(sketch, "E187", {"start": v(0, -482.6) * mm, "end": v(152.4, -482.6) * mm});
            skLineSegment(sketch, "E188", {"start": v(152.4, -482.6) * mm, "end": v(152.4, -152.4) * mm});
            skLineSegment(sketch, "E189", {"start": v(152.4, -152.4) * mm, "end": v(482.6, -152.4) * mm});
            skLineSegment(sketch, "E190", {"start": v(482.6, -152.4) * mm, "end": v(482.6, 0) * mm});
            skLineSegment(sketch, "E191", {"start": v(482.6, 0) * mm, "end": v(0, 0) * mm});
            skLineSegment(sketch, "E192", {"start": v(7645.4, 0) * mm, "end": v(7645.4, -482.6) * mm});
            skLineSegment(sketch, "E193", {"start": v(7645.4, -482.6) * mm, "end": v(7493, -482.6) * mm});
            skLineSegment(sketch, "E194", {"start": v(7493, -482.6) * mm, "end": v(7493, -152.4) * mm});
            skLineSegment(sketch, "E195", {"start": v(7493, -152.4) * mm, "end": v(7162.8, -152.4) * mm});
            skLineSegment(sketch, "E196", {"start": v(7162.8, -152.4) * mm, "end": v(7162.8, 0) * mm});
            skLineSegment(sketch, "E197", {"start": v(7162.8, 0) * mm, "end": v(7645.4, 0) * mm});
            skLineSegment(sketch, "E198", {"start": v(10363.2, -10541) * mm, "end": v(9880.6, -10541) * mm});
            skLineSegment(sketch, "E199", {"start": v(9880.6, -10541) * mm, "end": v(9880.6, -10693.4) * mm});
            skLineSegment(sketch, "E200", {"start": v(9880.6, -10693.4) * mm, "end": v(10210.8, -10693.4) * mm});
            skLineSegment(sketch, "E201", {"start": v(10210.8, -10693.4) * mm, "end": v(10210.8, -11023.6) * mm});
            skLineSegment(sketch, "E202", {"start": v(10210.8, -11023.6) * mm, "end": v(10363.2, -11023.6) * mm});
            skLineSegment(sketch, "E203", {"start": v(10363.2, -11023.6) * mm, "end": v(10363.2, -10541) * mm});
            skLineSegment(sketch, "E204", {"start": v(10363.2, -19075.4) * mm, "end": v(9880.6, -19075.4) * mm});
            skLineSegment(sketch, "E205", {"start": v(9880.6, -19075.4) * mm, "end": v(9880.6, -18923) * mm});
            skLineSegment(sketch, "E206", {"start": v(9880.6, -18923) * mm, "end": v(10210.8, -18923) * mm});
            skLineSegment(sketch, "E207", {"start": v(10210.8, -18923) * mm, "end": v(10210.8, -18592.8) * mm});
            skLineSegment(sketch, "E208", {"start": v(10210.8, -18592.8) * mm, "end": v(10363.2, -18592.8) * mm});
            skLineSegment(sketch, "E209", {"start": v(10363.2, -18592.8) * mm, "end": v(10363.2, -19075.4) * mm});
            skLineSegment(sketch, "E210", {"start": v(0, -23342.6) * mm, "end": v(0, -22860) * mm});
            skLineSegment(sketch, "E211", {"start": v(0, -22860) * mm, "end": v(152.4, -22860) * mm});
            skLineSegment(sketch, "E212", {"start": v(152.4, -22860) * mm, "end": v(152.4, -23190.2) * mm});
            skLineSegment(sketch, "E213", {"start": v(152.4, -23190.2) * mm, "end": v(482.6, -23190.2) * mm});
            skLineSegment(sketch, "E214", {"start": v(482.6, -23190.2) * mm, "end": v(482.6, -23342.6) * mm});
            skLineSegment(sketch, "E215", {"start": v(482.6, -23342.6) * mm, "end": v(0, -23342.6) * mm});
            skLineSegment(sketch, "E216", {"start": v(5486.4, -23342.6) * mm, "end": v(5486.4, -22860) * mm});
            skLineSegment(sketch, "E217", {"start": v(5486.4, -22860) * mm, "end": v(5334, -22860) * mm});
            skLineSegment(sketch, "E218", {"start": v(5334, -22860) * mm, "end": v(5334, -23190.2) * mm});
            skLineSegment(sketch, "E219", {"start": v(5334, -23190.2) * mm, "end": v(5003.8, -23190.2) * mm});
            skLineSegment(sketch, "E220", {"start": v(5003.8, -23190.2) * mm, "end": v(5003.8, -23342.6) * mm});
            skLineSegment(sketch, "E221", {"start": v(5003.8, -23342.6) * mm, "end": v(5486.4, -23342.6) * mm});
            skSolve(sketch);
        }
        {
            var Q0;
            Q0 = qSketchRegion(id + "F79", true);
            extrude(context, id + "F80", {"entities" : qUnion([Q0]), "operationType" : NewBodyOperationType.REMOVE, "oppositeDirection" : true, "depth" : 127 * mm});
        }
    });
